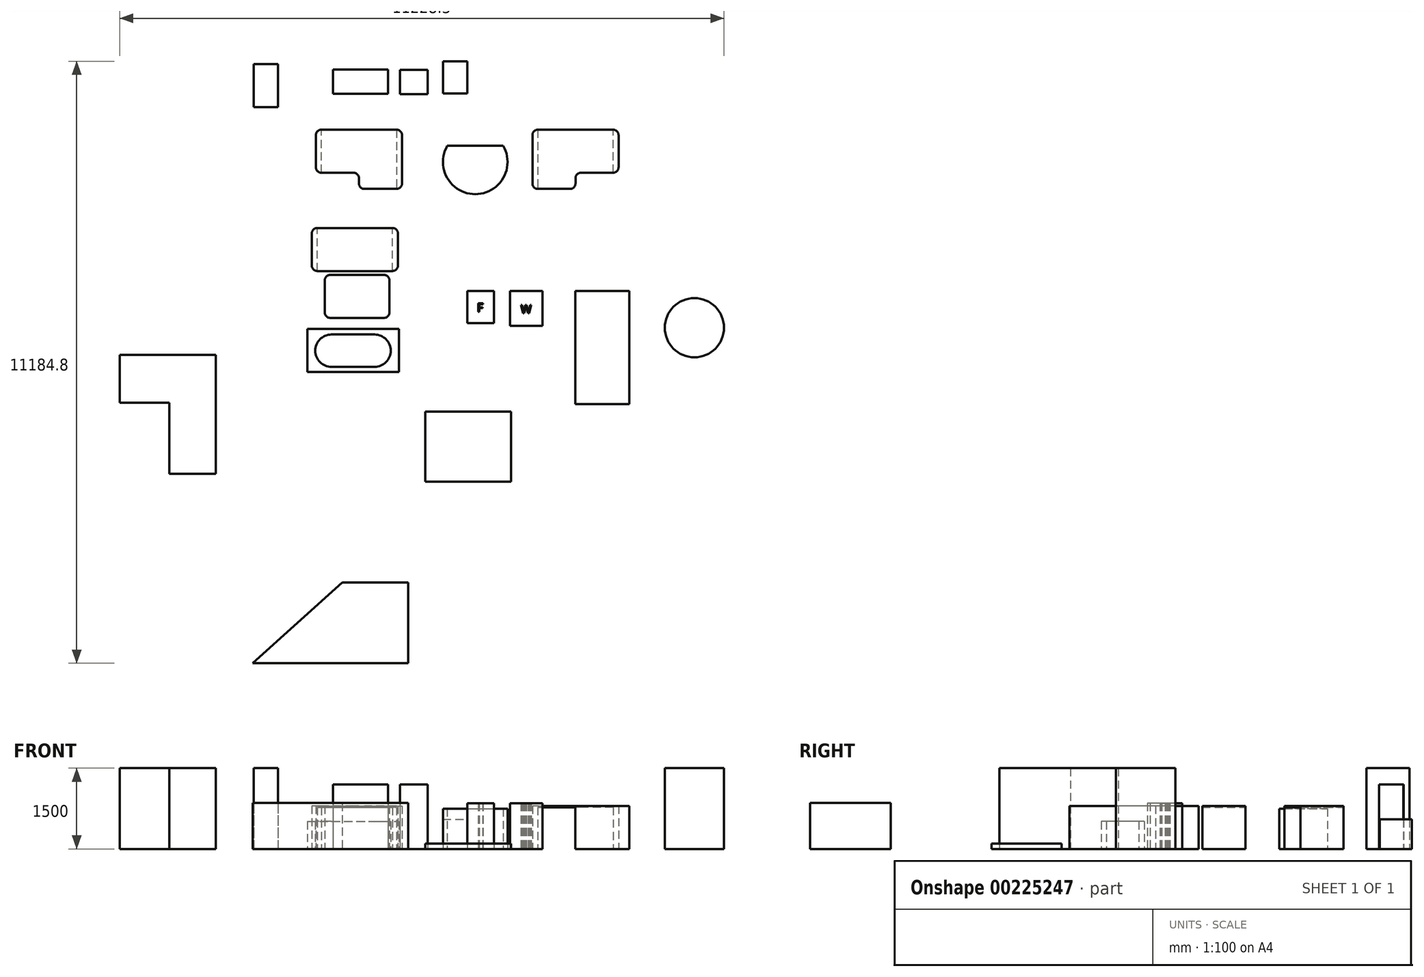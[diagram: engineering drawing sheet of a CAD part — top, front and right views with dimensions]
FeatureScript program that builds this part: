
annotation { "Feature Type Name" : "Feature", "Feature Type Description" : "" }
export const myFeature = defineFeature(function(context is Context, id is Id, definition is map)
    precondition{}
    {
        {
            var Q0;
            Q0=qCreatedBy(makeId("Top.planeOp"),FACE);
            var sketch = newSketch(context, id + "F0", { "sketchPlane" : qUnion([Q0])});
            skLineSegment(sketch, "E0.bottom", {"start": v(0, 0) * mm, "end": v(500, 0) * mm});
            skLineSegment(sketch, "E0.top", {"start": v(0, -600) * mm, "end": v(500, -600) * mm});
            skLineSegment(sketch, "E0.left", {"start": v(0, 0) * mm, "end": v(0, -600) * mm});
            skLineSegment(sketch, "E0.right", {"start": v(500, 0) * mm, "end": v(500, -600) * mm});
            skText(sketch, "E1", { "text": "F", "fontName": "OpenSans-Regular.ttf"});
            const initialGuessF0  = {"E1": [0.1838, -0.3865, 1, 0, 0.1581]};
            skSetInitialGuess(sketch, initialGuessF0);
            skSolve(sketch);
        }
        {
            var Q0;
            Q0 = qSketchRegion(id + "F0", true);
            extrude(context, id + "F1", {"entities" : qUnion([Q0]), "depth" : 850 * mm});
        }
        {
            var Q0;
            Q0=qCreatedBy(makeId("Top.planeOp"),FACE);
            var sketch = newSketch(context, id + "F2", { "sketchPlane" : qUnion([Q0])});
            skLineSegment(sketch, "E2.bottom", {"start": v(798.65, 0) * mm, "end": v(1398.65, 0) * mm});
            skLineSegment(sketch, "E2.top", {"start": v(798.65, -650) * mm, "end": v(1398.65, -650) * mm});
            skLineSegment(sketch, "E2.left", {"start": v(798.65, 0) * mm, "end": v(798.65, -650) * mm});
            skLineSegment(sketch, "E2.right", {"start": v(1398.65, 0) * mm, "end": v(1398.65, -650) * mm});
            skText(sketch, "E3", { "text": "W", "fontName": "OpenSans-Regular.ttf"});
            const initialGuessF2  = {"E3": [0.99336, -0.4146, 1, 0, 0.15712]};
            skSetInitialGuess(sketch, initialGuessF2);
            skSolve(sketch);
        }
        {
            var Q0;
            Q0 = qSketchRegion(id + "F2", true);
            extrude(context, id + "F3", {"entities" : qUnion([Q0]), "depth" : 850 * mm});
        }
        {
            var Q0;
            Q0=qCreatedBy(makeId("Top.planeOp"),FACE);
            var sketch = newSketch(context, id + "F4", { "sketchPlane" : qUnion([Q0])});
            skLineSegment(sketch, "E4.bottom", {"start": v(2008.64, 0) * mm, "end": v(3008.64, 0) * mm});
            skLineSegment(sketch, "E4.top", {"start": v(2008.64, -2100) * mm, "end": v(3008.64, -2100) * mm});
            skLineSegment(sketch, "E4.left", {"start": v(2008.64, 0) * mm, "end": v(2008.64, -2100) * mm});
            skLineSegment(sketch, "E4.right", {"start": v(3008.64, 0) * mm, "end": v(3008.64, -2100) * mm});
            skSolve(sketch);
        }
        {
            var Q0;
            Q0 = qSketchRegion(id + "F4", true);
            extrude(context, id + "F5", {"entities" : qUnion([Q0]), "depth" : 800 * mm});
        }
        {
            var Q0;
            Q0=qCreatedBy(makeId("Top.planeOp"),FACE);
            var sketch = newSketch(context, id + "F6", { "sketchPlane" : qUnion([Q0])});
            skCircle(sketch, "E5", {"center": v(4221.71, -682.9) * mm, "radius": 550 * mm});
            skSolve(sketch);
        }
        {
            var Q0;
            Q0 = qSketchRegion(id + "F6", true);
            extrude(context, id + "F7", {"entities" : qUnion([Q0]), "depth" : 1500 * mm});
        }
        {
            var Q0;
            Q0=qCreatedBy(makeId("Top.planeOp"),FACE);
            var sketch = newSketch(context, id + "F8", { "sketchPlane" : qUnion([Q0])});
            skLineSegment(sketch, "E6.bottom", {"start": v(-2969.72, -707.9) * mm, "end": v(-1269.72, -707.9) * mm});
            skLineSegment(sketch, "E6.top", {"start": v(-2969.72, -1507.9) * mm, "end": v(-1269.72, -1507.9) * mm});
            skLineSegment(sketch, "E6.left", {"start": v(-2969.72, -707.9) * mm, "end": v(-2969.72, -1507.9) * mm});
            skLineSegment(sketch, "E6.right", {"start": v(-1269.72, -707.9) * mm, "end": v(-1269.72, -1507.9) * mm});
            skLineSegment(sketch, "E7", {"start": v(-2522.87, -1109.61) * mm, "end": v(-1719.37, -1109.61) * mm});
            skArc(sketch, "E8.0.startCap", {"start": v(-2522.87, -1409.61) * mm, "mid": v(-2822.87, -1109.61) * mm, "end": v(-2522.87, -809.61) * mm});
            skArc(sketch, "E8.0.endCap", {"start": v(-1719.37, -809.61) * mm, "mid": v(-1419.37, -1109.61) * mm, "end": v(-1719.37, -1409.61) * mm});
            skLineSegment(sketch, "E8.0.left", {"start": v(-2522.87, -809.61) * mm, "end": v(-1719.37, -809.61) * mm});
            skLineSegment(sketch, "E8.0.right", {"start": v(-2522.87, -1409.61) * mm, "end": v(-1719.37, -1409.61) * mm});
            skSolve(sketch);
        }
        {
            var Q0;
            Q0=makeQuery(id+"F8.imprint","IMPRINT",FACE,{"disambiguationData":[TD([[makeQuery(id+"F8.imprint","IMPRINT",EDGE,{"derivedFrom":sQuery(id+"F8.wireOp",EDGE,"E6.bottom")}),-1.0]])]});
            extrude(context, id + "F9", {"entities" : qUnion([Q0]), "depth" : 510 * mm});
        }
        {
            var Q0;
            Q0=qCreatedBy(makeId("Top.planeOp"),FACE);
            var sketch = newSketch(context, id + "F10", { "sketchPlane" : qUnion([Q0])});
            skLineSegment(sketch, "E9", {"start": v(-3986.57, -6917.17) * mm, "end": v(-1098.98, -4317.17) * mm});
            skLineSegment(sketch, "E10", {"start": v(-1098.98, -4317.17) * mm, "end": v(-1098.98, -6917.17) * mm});
            skLineSegment(sketch, "E11", {"start": v(-1098.98, -6917.17) * mm, "end": v(-3986.57, -6917.17) * mm});
            skLineSegment(sketch, "E12", {"start": v(-3986.57, -6917.17) * mm, "end": v(-3986.57, -6017.17) * mm});
            skLineSegment(sketch, "E13", {"start": v(-3986.57, -6017.17) * mm, "end": v(-1098.98, -3417.17) * mm});
            skLineSegment(sketch, "E14", {"start": v(-1098.98, -3417.17) * mm, "end": v(-1098.98, -4317.17) * mm});
            skLineSegment(sketch, "E15", {"start": v(-3986.57, -6917.17) * mm, "end": v(-3986.57, -7772.17) * mm});
            skLineSegment(sketch, "E16", {"start": v(-3986.57, -7772.17) * mm, "end": v(-1098.98, -7772.17) * mm});
            skLineSegment(sketch, "E17", {"start": v(-1098.98, -7772.17) * mm, "end": v(-1098.98, -6917.17) * mm});
            skLineSegment(sketch, "E18", {"start": v(-1098.98, -5417.17) * mm, "end": v(-2320.66, -5417.17) * mm});
            skSolve(sketch);
        }
        {
            var Q0;
            {var subQ0=sQuery(id+"F10.wireOp",EDGE,"E11");Q0=makeQuery(id+"F10.imprint","IMPRINT",FACE,{"disambiguationData":[TD([[makeQuery(id+"F10.imprint","IMPRINT",EDGE,{"derivedFrom":subQ0}),-1.0]])]});}
            extrude(context, id + "F11", {"entities" : qUnion([Q0]), "depth" : 855 * mm});
        }
        {
            var Q0;
            Q0=qCreatedBy(makeId("Top.planeOp"),FACE);
            var sketch = newSketch(context, id + "F12", { "sketchPlane" : qUnion([Q0])});
            skLineSegment(sketch, "E19.bottom", {"start": v(-781.7, -2243.4) * mm, "end": v(811.9, -2243.4) * mm});
            skLineSegment(sketch, "E19.top", {"start": v(-781.7, -3543.3) * mm, "end": v(811.9, -3543.3) * mm});
            skLineSegment(sketch, "E19.left", {"start": v(-781.7, -2243.4) * mm, "end": v(-781.7, -3543.3) * mm});
            skLineSegment(sketch, "E19.right", {"start": v(811.9, -2243.4) * mm, "end": v(811.9, -3543.3) * mm});
            skSolve(sketch);
        }
        {
            var Q0;
            Q0=makeQuery(id+"F12.imprint","IMPRINT",FACE,{"disambiguationData":[TD([[makeQuery(id+"F12.imprint","IMPRINT",EDGE,{"derivedFrom":sQuery(id+"F12.wireOp",EDGE,"E19.bottom")}),-1.0]])]});
            extrude(context, id + "F13", {"entities" : qUnion([Q0]), "depth" : 100 * mm});
        }
        {
            var Q0;
            Q0=qCreatedBy(makeId("Top.planeOp"),FACE);
            var sketch = newSketch(context, id + "F14", { "sketchPlane" : qUnion([Q0])});
            skLineSegment(sketch, "E20.bottom", {"start": v(-2786.97, 1170.78) * mm, "end": v(-1386.97, 1170.78) * mm});
            skLineSegment(sketch, "E20.top", {"start": v(-2786.97, 370.78) * mm, "end": v(-1386.97, 370.78) * mm});
            skLineSegment(sketch, "E20.left", {"start": v(-2886.97, 1070.78) * mm, "end": v(-2886.97, 470.78) * mm});
            skLineSegment(sketch, "E20.right", {"start": v(-1286.97, 1070.78) * mm, "end": v(-1286.97, 470.78) * mm});
            skPoint(sketch, "E21.visualSharp", {"position": v(-1286.97, 1170.78) * mm});
            skArc(sketch, "E21.filletArc", {"start": v(-1286.97, 1070.78) * mm, "mid": v(-1316.25, 1141.49) * mm, "end": v(-1386.97, 1170.78) * mm});
            skPoint(sketch, "E22.visualSharp", {"position": v(-1286.97, 370.78) * mm});
            skArc(sketch, "E22.filletArc", {"start": v(-1386.97, 370.78) * mm, "mid": v(-1316.25, 400.07) * mm, "end": v(-1286.97, 470.78) * mm});
            skPoint(sketch, "E23.visualSharp", {"position": v(-2886.97, 370.78) * mm});
            skArc(sketch, "E23.filletArc", {"start": v(-2886.97, 470.78) * mm, "mid": v(-2857.68, 400.07) * mm, "end": v(-2786.97, 370.78) * mm});
            skPoint(sketch, "E24.visualSharp", {"position": v(-2886.97, 1170.78) * mm});
            skArc(sketch, "E24.filletArc", {"start": v(-2786.97, 1170.78) * mm, "mid": v(-2857.68, 1141.49) * mm, "end": v(-2886.97, 1070.78) * mm});
            skSolve(sketch);
        }
        {
            var Q0;
            Q0 = qSketchRegion(id + "F14", true);
            extrude(context, id + "F15", {"entities" : qUnion([Q0]), "depth" : 800 * mm});
        }
        {
            var Q0;
            Q0=qCreatedBy(makeId("Top.planeOp"),FACE);
            var sketch = newSketch(context, id + "F16", { "sketchPlane" : qUnion([Q0])});
            skLineSegment(sketch, "E25", {"start": v(-2711.98, 2996.95) * mm, "end": v(-1311.98, 2996.95) * mm});
            skLineSegment(sketch, "E26", {"start": v(-1211.98, 2896.95) * mm, "end": v(-1211.98, 1996.95) * mm});
            skLineSegment(sketch, "E27", {"start": v(-1311.98, 1896.95) * mm, "end": v(-1911.98, 1896.95) * mm});
            skLineSegment(sketch, "E28", {"start": v(-2011.98, 1996.95) * mm, "end": v(-2011.98, 2096.95) * mm});
            skLineSegment(sketch, "E29", {"start": v(-2111.98, 2196.95) * mm, "end": v(-2711.98, 2196.95) * mm});
            skLineSegment(sketch, "E30", {"start": v(-2811.98, 2296.95) * mm, "end": v(-2811.98, 2896.95) * mm});
            skPoint(sketch, "E31.visualSharp", {"position": v(-2811.98, 2996.95) * mm});
            skArc(sketch, "E31.filletArc", {"start": v(-2711.98, 2996.95) * mm, "mid": v(-2782.7, 2967.66) * mm, "end": v(-2811.98, 2896.95) * mm});
            skPoint(sketch, "E32.visualSharp", {"position": v(-2811.98, 2196.95) * mm});
            skArc(sketch, "E32.filletArc", {"start": v(-2811.98, 2296.95) * mm, "mid": v(-2782.7, 2226.24) * mm, "end": v(-2711.98, 2196.95) * mm});
            skPoint(sketch, "E33.visualSharp", {"position": v(-2011.98, 2196.95) * mm});
            skArc(sketch, "E33.filletArc", {"start": v(-2011.98, 2096.95) * mm, "mid": v(-2041.27, 2167.66) * mm, "end": v(-2111.98, 2196.95) * mm});
            skPoint(sketch, "E34.visualSharp", {"position": v(-2011.98, 1896.95) * mm});
            skArc(sketch, "E34.filletArc", {"start": v(-2011.98, 1996.95) * mm, "mid": v(-1982.7, 1926.24) * mm, "end": v(-1911.98, 1896.95) * mm});
            skPoint(sketch, "E35.visualSharp", {"position": v(-1211.98, 1896.95) * mm});
            skArc(sketch, "E35.filletArc", {"start": v(-1311.98, 1896.95) * mm, "mid": v(-1241.27, 1926.24) * mm, "end": v(-1211.98, 1996.95) * mm});
            skPoint(sketch, "E36.visualSharp", {"position": v(-1211.98, 2996.95) * mm});
            skArc(sketch, "E36.filletArc", {"start": v(-1211.98, 2896.95) * mm, "mid": v(-1241.27, 2967.66) * mm, "end": v(-1311.98, 2996.95) * mm});
            skSolve(sketch);
        }
        {
            var Q0;
            Q0=makeQuery(id+"F16.imprint","IMPRINT",FACE,{"disambiguationData":[TD([[makeQuery(id+"F16.imprint","IMPRINT",EDGE,{"derivedFrom":sQuery(id+"F16.wireOp",EDGE,"E25")}),-1.0]])]});
            extrude(context, id + "F17", {"entities" : qUnion([Q0]), "depth" : 800 * mm});
        }
        {
            var Q0;
            Q0=qCreatedBy(makeId("Top.planeOp"),FACE);
            var sketch = newSketch(context, id + "F18", { "sketchPlane" : qUnion([Q0])});
            skLineSegment(sketch, "E37.bottom", {"start": v(-2492.86, 4112.49) * mm, "end": v(-1472.86, 4112.49) * mm});
            skLineSegment(sketch, "E37.top", {"start": v(-2492.86, 3662.49) * mm, "end": v(-1472.86, 3662.49) * mm});
            skLineSegment(sketch, "E37.left", {"start": v(-2492.86, 4112.49) * mm, "end": v(-2492.86, 3662.49) * mm});
            skLineSegment(sketch, "E37.right", {"start": v(-1472.86, 4112.49) * mm, "end": v(-1472.86, 3662.49) * mm});
            skSolve(sketch);
        }
        {
            var Q0;
            Q0 = qSketchRegion(id + "F18", true);
            extrude(context, id + "F19", {"entities" : qUnion([Q0]), "depth" : 1200 * mm});
        }
        {
            var Q0;
            Q0=qCreatedBy(makeId("Top.planeOp"),FACE);
            var sketch = newSketch(context, id + "F20", { "sketchPlane" : qUnion([Q0])});
            skCircle(sketch, "E38", {"center": v(149.65, 2398.65) * mm, "radius": 600 * mm});
            skLineSegment(sketch, "E39", {"start": v(-369.96, 2698.65) * mm, "end": v(669.27, 2698.65) * mm});
            skLineSegment(sketch, "E40", {"start": v(-369.96, 2098.65) * mm, "end": v(669.27, 2098.65) * mm});
            skLineSegment(sketch, "E41", {"start": v(-450.35, 2398.65) * mm, "end": v(749.65, 2398.65) * mm, "construction": true});
            skSolve(sketch);
        }
        {
            var Q0;
            {var subQ0=sQuery(id+"F20.wireOp",EDGE,"E40");Q0=makeQuery(id+"F20.imprint","IMPRINT",FACE,{"disambiguationData":[TD([[makeQuery(id+"F20.imprint","IMPRINT",EDGE,{"derivedFrom":subQ0}),-1.0]])]});}
            var Q1;
            {var subQ0=sQuery(id+"F20.wireOp",EDGE,"E39");Q1=makeQuery(id+"F20.imprint","IMPRINT",FACE,{"disambiguationData":[TD([[makeQuery(id+"F20.imprint","IMPRINT",EDGE,{"derivedFrom":subQ0}),-1.0]])]});}
            extrude(context, id + "F21", {"entities" : qUnion([Q0, Q1]), "depth" : 750 * mm});
        }
        {
            var Q0;
            Q0=qCreatedBy(makeId("Top.planeOp"),FACE);
            var sketch = newSketch(context, id + "F22", { "sketchPlane" : qUnion([Q0])});
            skLineSegment(sketch, "E42.bottom", {"start": v(-2546.18, 299.35) * mm, "end": v(-1546.18, 299.35) * mm});
            skLineSegment(sketch, "E42.top", {"start": v(-2546.18, -500.65) * mm, "end": v(-1546.18, -500.65) * mm});
            skLineSegment(sketch, "E42.left", {"start": v(-2646.18, 199.35) * mm, "end": v(-2646.18, -400.65) * mm});
            skLineSegment(sketch, "E42.right", {"start": v(-1446.18, 199.35) * mm, "end": v(-1446.18, -400.65) * mm});
            skPoint(sketch, "E43.visualSharp", {"position": v(-1446.18, -500.65) * mm});
            skArc(sketch, "E43.filletArc", {"start": v(-1546.18, -500.65) * mm, "mid": v(-1475.47, -471.36) * mm, "end": v(-1446.18, -400.65) * mm});
            skPoint(sketch, "E44.visualSharp", {"position": v(-2646.18, -500.65) * mm});
            skArc(sketch, "E44.filletArc", {"start": v(-2646.18, -400.65) * mm, "mid": v(-2616.9, -471.36) * mm, "end": v(-2546.18, -500.65) * mm});
            skPoint(sketch, "E45.visualSharp", {"position": v(-2646.18, 299.35) * mm});
            skArc(sketch, "E45.filletArc", {"start": v(-2546.18, 299.35) * mm, "mid": v(-2616.9, 270.06) * mm, "end": v(-2646.18, 199.35) * mm});
            skPoint(sketch, "E46.visualSharp", {"position": v(-1446.18, 299.35) * mm});
            skArc(sketch, "E46.filletArc", {"start": v(-1446.18, 199.35) * mm, "mid": v(-1475.47, 270.06) * mm, "end": v(-1546.18, 299.35) * mm});
            skSolve(sketch);
        }
        {
            var Q0;
            Q0=makeQuery(id+"F22.imprint","IMPRINT",FACE,{"disambiguationData":[TD([[makeQuery(id+"F22.imprint","IMPRINT",EDGE,{"derivedFrom":sQuery(id+"F22.wireOp",EDGE,"E42.bottom")}),-1.0]])]});
            extrude(context, id + "F23", {"entities" : qUnion([Q0]), "depth" : 800 * mm});
        }
        {
            var Q0;
            Q0=qCreatedBy(makeId("Top.planeOp"),FACE);
            var sketch = newSketch(context, id + "F24", { "sketchPlane" : qUnion([Q0])});
            skLineSegment(sketch, "E47.bottom", {"start": v(-1246.23, 4106.9) * mm, "end": v(-736.23, 4106.9) * mm});
            skLineSegment(sketch, "E47.top", {"start": v(-1246.23, 3656.9) * mm, "end": v(-736.23, 3656.9) * mm});
            skLineSegment(sketch, "E47.left", {"start": v(-1246.23, 4106.9) * mm, "end": v(-1246.23, 3656.9) * mm});
            skLineSegment(sketch, "E47.right", {"start": v(-736.23, 4106.9) * mm, "end": v(-736.23, 3656.9) * mm});
            skSolve(sketch);
        }
        {
            var Q0;
            Q0=makeQuery(id+"F24.imprint","IMPRINT",FACE,{"disambiguationData":[TD([[makeQuery(id+"F24.imprint","IMPRINT",EDGE,{"derivedFrom":sQuery(id+"F24.wireOp",EDGE,"E47.bottom")}),-1.0]])]});
            extrude(context, id + "F25", {"entities" : qUnion([Q0]), "depth" : 1200 * mm});
        }
        {
            var Q0;
            Q0=qCreatedBy(makeId("Top.planeOp"),FACE);
            var sketch = newSketch(context, id + "F26", { "sketchPlane" : qUnion([Q0])});
            skLineSegment(sketch, "E48.bottom", {"start": v(-450, 4267.62) * mm, "end": v(0, 4267.62) * mm});
            skLineSegment(sketch, "E48.top", {"start": v(-450, 3667.62) * mm, "end": v(0, 3667.62) * mm});
            skLineSegment(sketch, "E48.left", {"start": v(-450, 4267.62) * mm, "end": v(-450, 3667.62) * mm});
            skLineSegment(sketch, "E48.right", {"start": v(0, 4267.62) * mm, "end": v(0, 3667.62) * mm});
            skSolve(sketch);
        }
        {
            var Q0;
            Q0=makeQuery(id+"F26.imprint","IMPRINT",FACE,{"disambiguationData":[TD([[makeQuery(id+"F26.imprint","IMPRINT",EDGE,{"derivedFrom":sQuery(id+"F26.wireOp",EDGE,"E48.bottom")}),-1.0]])]});
            extrude(context, id + "F27", {"entities" : qUnion([Q0]), "depth" : 550 * mm});
        }
        {
            var Q0;
            Q0=makeQuery(id+"F15.opExtrude","CAP_FACE",FACE,{"disambiguationData":[OSD([sQuery(id+"F14.wireOp",EDGE,"E20.bottom"),sQuery(id+"F14.wireOp",EDGE,"E20.top"),sQuery(id+"F14.wireOp",EDGE,"E20.left"),sQuery(id+"F14.wireOp",EDGE,"E20.right"),sQuery(id+"F14.wireOp",EDGE,"E21.filletArc"),sQuery(id+"F14.wireOp",EDGE,"E22.filletArc"),sQuery(id+"F14.wireOp",EDGE,"E23.filletArc"),sQuery(id+"F14.wireOp",EDGE,"E24.filletArc")])],"isStart":true});
            var sketch = newSketch(context, id + "F28", { "sketchPlane" : qUnion([Q0])});
            skLineSegment(sketch, "E49.bottom", {"start": v(-2786.97, -370.78) * mm, "end": v(-1386.97, -370.78) * mm});
            skLineSegment(sketch, "E49.top", {"start": v(-2786.97, -1170.78) * mm, "end": v(-1386.97, -1170.78) * mm});
            skLineSegment(sketch, "E49.left", {"start": v(-2786.97, -370.78) * mm, "end": v(-2786.97, -1170.78) * mm});
            skLineSegment(sketch, "E49.right", {"start": v(-1386.97, -370.78) * mm, "end": v(-1386.97, -1170.78) * mm});
            skSolve(sketch);
        }
        {
            var Q0;
            Q0=makeQuery(id+"F28.imprint","IMPRINT",FACE,{"disambiguationData":[TD([[makeQuery(id+"F28.imprint","IMPRINT",EDGE,{"derivedFrom":sQuery(id+"F28.wireOp",EDGE,"E49.bottom")}),-1.0]])]});
            var Q1;
            Q1 = qSketchRegion(id + "F28", true);
            extrude(context, id + "F29", {"entities" : qUnion([Q0, Q1]), "operationType" : NewBodyOperationType.REMOVE, "oppositeDirection" : true, "depth" : 775 * mm});
        }
        {
            var Q0;
            Q0=makeQuery(id+"F17.opExtrude","CAP_FACE",FACE,{"disambiguationData":[OSD([sQuery(id+"F16.wireOp",EDGE,"E25"),sQuery(id+"F16.wireOp",EDGE,"E26"),sQuery(id+"F16.wireOp",EDGE,"E27"),sQuery(id+"F16.wireOp",EDGE,"E28"),sQuery(id+"F16.wireOp",EDGE,"E29"),sQuery(id+"F16.wireOp",EDGE,"E30"),sQuery(id+"F16.wireOp",EDGE,"E31.filletArc"),sQuery(id+"F16.wireOp",EDGE,"E32.filletArc"),sQuery(id+"F16.wireOp",EDGE,"E33.filletArc"),sQuery(id+"F16.wireOp",EDGE,"E34.filletArc"),sQuery(id+"F16.wireOp",EDGE,"E35.filletArc"),sQuery(id+"F16.wireOp",EDGE,"E36.filletArc")])],"isStart":true});
            var sketch = newSketch(context, id + "F30", { "sketchPlane" : qUnion([Q0])});
            skLineSegment(sketch, "E50", {"start": v(-2711.98, -2196.95) * mm, "end": v(-2711.98, -2996.95) * mm});
            skLineSegment(sketch, "E51", {"start": v(-2711.98, -2996.95) * mm, "end": v(-1311.98, -2996.95) * mm});
            skLineSegment(sketch, "E52", {"start": v(-1311.98, -2996.95) * mm, "end": v(-1311.98, -1896.95) * mm});
            skLineSegment(sketch, "E53", {"start": v(-1311.98, -1896.95) * mm, "end": v(-2711.98, -1896.95) * mm});
            skPoint(sketch, "E53.endSnap0", {"position": v(-1983, -1896.95) * mm});
            skLineSegment(sketch, "E54", {"start": v(-2711.98, -1896.95) * mm, "end": v(-2711.98, -2196.95) * mm});
            skSolve(sketch);
        }
        {
            var Q0;
            Q0 = qSketchRegion(id + "F30", true);
            extrude(context, id + "F31", {"entities" : qUnion([Q0]), "operationType" : NewBodyOperationType.REMOVE, "oppositeDirection" : true, "depth" : 775 * mm});
        }
        {
            var Q0;
            Q0=makeQuery(id+"F17.opExtrude","SWEPT_BODY",BODY,{"disambiguationData":[OSD([sQuery(id+"F16.wireOp",EDGE,"E25"),sQuery(id+"F16.wireOp",EDGE,"E26"),sQuery(id+"F16.wireOp",EDGE,"E27"),sQuery(id+"F16.wireOp",EDGE,"E28"),sQuery(id+"F16.wireOp",EDGE,"E29"),sQuery(id+"F16.wireOp",EDGE,"E30"),sQuery(id+"F16.wireOp",EDGE,"E31.filletArc"),sQuery(id+"F16.wireOp",EDGE,"E32.filletArc"),sQuery(id+"F16.wireOp",EDGE,"E33.filletArc"),sQuery(id+"F16.wireOp",EDGE,"E34.filletArc"),sQuery(id+"F16.wireOp",EDGE,"E35.filletArc"),sQuery(id+"F16.wireOp",EDGE,"E36.filletArc")])]});
            var Q1;
            Q1=qCreatedBy(makeId("Right.planeOp"),FACE);
            mirror(context, id + "F32", {"entities" : qUnion([Q0]), "mirrorPlane" : qUnion([Q1])});
        }
        {
            var Q0;
            Q0=qCreatedBy(makeId("Top.planeOp"),FACE);
            var sketch = newSketch(context, id + "F33", { "sketchPlane" : qUnion([Q0])});
            skLineSegment(sketch, "E55.bottom", {"start": v(-3969.02, 4217.39) * mm, "end": v(-3519.02, 4217.39) * mm});
            skLineSegment(sketch, "E55.top", {"start": v(-3969.02, 3417.39) * mm, "end": v(-3519.02, 3417.39) * mm});
            skLineSegment(sketch, "E55.left", {"start": v(-3969.02, 4217.39) * mm, "end": v(-3969.02, 3417.39) * mm});
            skLineSegment(sketch, "E55.right", {"start": v(-3519.02, 4217.39) * mm, "end": v(-3519.02, 3417.39) * mm});
            skSolve(sketch);
        }
        {
            var Q0;
            Q0=makeQuery(id+"F33.imprint","IMPRINT",FACE,{"disambiguationData":[TD([[makeQuery(id+"F33.imprint","IMPRINT",EDGE,{"derivedFrom":sQuery(id+"F33.wireOp",EDGE,"E55.bottom")}),-1.0]])]});
            extrude(context, id + "F34", {"entities" : qUnion([Q0]), "depth" : 1500 * mm});
        }
        {
            var Q0;
            Q0=qCreatedBy(makeId("Top.planeOp"),FACE);
            var sketch = newSketch(context, id + "F35", { "sketchPlane" : qUnion([Q0])});
            skLineSegment(sketch, "E56.bottom", {"start": v(-6456.63, -1188.65) * mm, "end": v(-4668.63, -1188.65) * mm});
            skLineSegment(sketch, "E56.top", {"start": v(-5533.63, -3397.65) * mm, "end": v(-4668.63, -3397.65) * mm});
            skLineSegment(sketch, "E56.left", {"start": v(-6456.63, -1188.65) * mm, "end": v(-6456.63, -2077.65) * mm});
            skLineSegment(sketch, "E56.right", {"start": v(-4668.63, -1188.65) * mm, "end": v(-4668.63, -3397.65) * mm});
            skLineSegment(sketch, "E57", {"start": v(-5533.63, -3397.65) * mm, "end": v(-5533.63, -2077.65) * mm});
            skLineSegment(sketch, "E58", {"start": v(-5533.63, -2077.65) * mm, "end": v(-6456.63, -2077.65) * mm});
            skPoint(sketch, "E59.orphan", {"position": v(-6456.63, -3397.65) * mm});
            skSolve(sketch);
        }
        {
            var Q0;
            Q0 = qSketchRegion(id + "F35", true);
            extrude(context, id + "F36", {"entities" : qUnion([Q0]), "depth" : 1500 * mm});
        }
    });
